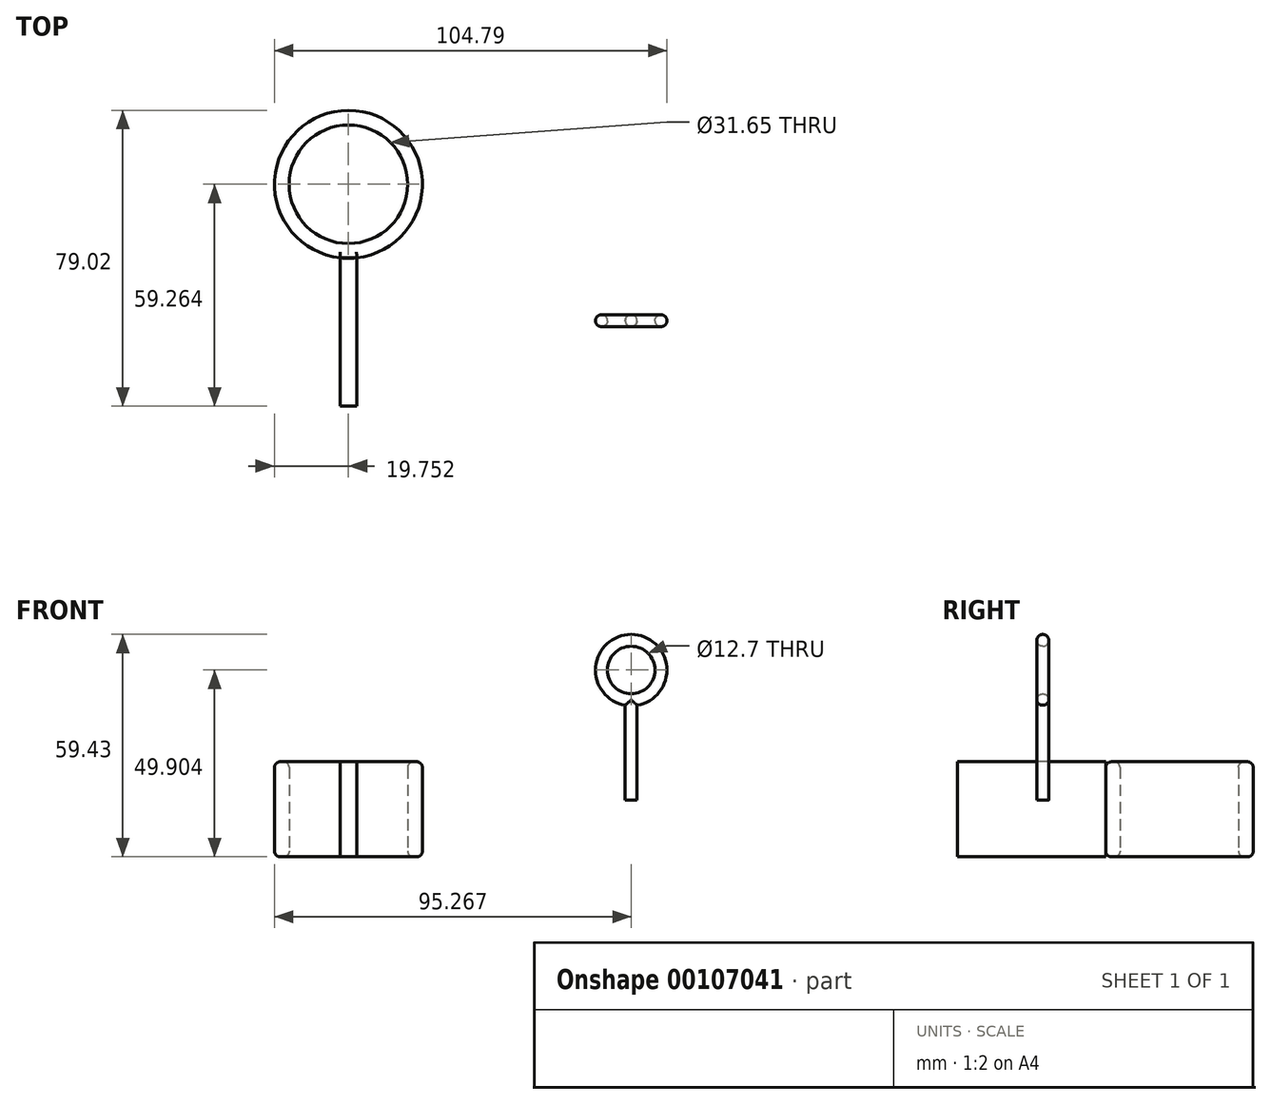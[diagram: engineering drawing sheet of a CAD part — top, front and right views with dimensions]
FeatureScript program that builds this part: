
annotation { "Feature Type Name" : "Feature", "Feature Type Description" : "" }
export const myFeature = defineFeature(function(context is Context, id is Id, definition is map)
    precondition{}
    {
        {
            var Q0;
            Q0=qCreatedBy(makeId("Top.planeOp"),FACE);
            var sketch = newSketch(context, id + "F0", { "sketchPlane" : qUnion([Q0])});
            skCircle(sketch, "E0", {"center": v(-17.5, 34.85) * mm, "radius": 15.83 * mm});
            skCircle(sketch, "E1", {"center": v(-17.5, 34.85) * mm, "radius": 19.76 * mm});
            skLineSegment(sketch, "E2.bottom", {"start": v(-19.74, 15.23) * mm, "end": v(-15.26, 15.23) * mm});
            skLineSegment(sketch, "E2.top", {"start": v(-19.74, -24.41) * mm, "end": v(-15.26, -24.41) * mm});
            skLineSegment(sketch, "E2.left", {"start": v(-19.74, 15.23) * mm, "end": v(-19.74, -24.41) * mm});
            skLineSegment(sketch, "E2.right", {"start": v(-15.26, 15.23) * mm, "end": v(-15.26, -24.41) * mm});
            skSolve(sketch);
        }
        {
            var Q0;
            Q0=makeQuery(id+"F0.imprint","IMPRINT",FACE,{"disambiguationData":[TD([[makeQuery(id+"F0.imprint","IMPRINT",EDGE,{"derivedFrom":sQuery(id+"F0.wireOp",EDGE,"E2.top")}),1.0]])]});
            var Q1;
            Q1=makeQuery(id+"F0.imprint","IMPRINT",FACE,{"disambiguationData":[TD([[makeQuery(id+"F0.imprint","IMPRINT",EDGE,{"derivedFrom":sQuery(id+"F0.wireOp",EDGE,"E0")}),-1.0]])]});
            extrude(context, id + "F1", {"entities" : qUnion([Q0, Q1]), "depth" : 25.4 * mm});
        }
        {
            var Q0;
            Q0=makeQuery(id+"F1.opExtrude","CAP_FACE",FACE,{"disambiguationData":[OSD([sQuery(id+"F0.wireOp",EDGE,"E0"),sQuery(id+"F0.wireOp",EDGE,"E1"),sQuery(id+"F0.wireOp",EDGE,"E2.bottom")])],"isStart":true});
            var Q1;
            Q1=makeQuery(id+"F1.opExtrude","CAP_EDGE",EDGE,{"disambiguationData":[OSD([sQuery(id+"F0.wireOp",EDGE,"E0")])],"isStart":false});
            var Q2;
            Q2=makeQuery(id+"F1.opExtrude","CAP_FACE",FACE,{"disambiguationData":[OSD([sQuery(id+"F0.wireOp",EDGE,"E0"),sQuery(id+"F0.wireOp",EDGE,"E1"),sQuery(id+"F0.wireOp",EDGE,"E2.bottom")])],"isStart":false});
            fillet(context, id + "F2", {"entities" : qUnion([Q0, Q1, Q2]), "radius" : 1.53 * mm, "tangentPropagation" : true, "allowEdgeOverflow" : false});
        }
        {
            var Q0;
            Q0=qCreatedBy(makeId("Front.planeOp"),FACE);
            var sketch = newSketch(context, id + "F3", { "sketchPlane" : qUnion([Q0])});
            skCircle(sketch, "E3", {"center": v(58.02, 49.9) * mm, "radius": 6.35 * mm});
            skCircle(sketch, "E4", {"center": v(58.02, 49.9) * mm, "radius": 9.53 * mm});
            skLineSegment(sketch, "E5", {"start": v(56.43, 40.51) * mm, "end": v(56.43, 15.11) * mm});
            skLineSegment(sketch, "E6", {"start": v(56.43, 15.11) * mm, "end": v(59.6, 15.11) * mm});
            skLineSegment(sketch, "E7", {"start": v(59.6, 15.11) * mm, "end": v(59.6, 40.51) * mm});
            skSolve(sketch);
        }
        {
            var Q0;
            {var subQ0=sQuery(id+"F3.wireOp",EDGE,"E5");Q0=makeQuery(id+"F3.imprint","IMPRINT",FACE,{"disambiguationData":[TD([[makeQuery(id+"F3.imprint","IMPRINT",EDGE,{"derivedFrom":subQ0}),1.0]])]});}
            var Q1;
            Q1=makeQuery(id+"F3.imprint","IMPRINT",FACE,{"disambiguationData":[TD([[makeQuery(id+"F3.imprint","IMPRINT",EDGE,{"derivedFrom":sQuery(id+"F3.wireOp",EDGE,"E3")}),-1.0]])]});
            extrude(context, id + "F4", {"entities" : qUnion([Q0, Q1]), "depth" : 3.17 * mm});
        }
        {
            var Q0;
            Q0=makeQuery(id+"F4.opExtrude","CAP_EDGE",EDGE,{"disambiguationData":[OSD([sQuery(id+"F3.wireOp",EDGE,"E3")])],"isStart":false});
            var Q1;
            Q1=makeQuery(id+"F4.opExtrude","CAP_EDGE",EDGE,{"disambiguationData":[OSD([sQuery(id+"F3.wireOp",EDGE,"E4")])],"isStart":false});
            var Q2;
            Q2=makeQuery(id+"F4.opExtrude","CAP_EDGE",EDGE,{"disambiguationData":[OSD([sQuery(id+"F3.wireOp",EDGE,"E7")])],"isStart":false});
            var Q3;
            Q3=makeQuery(id+"F4.opExtrude","CAP_EDGE",EDGE,{"disambiguationData":[OSD([sQuery(id+"F3.wireOp",EDGE,"E5")])],"isStart":false});
            var Q4;
            Q4=makeQuery(id+"F4.opExtrude","CAP_EDGE",EDGE,{"disambiguationData":[OSD([sQuery(id+"F3.wireOp",EDGE,"E4")])],"isStart":true});
            var Q5;
            Q5=makeQuery(id+"F4.opExtrude","CAP_EDGE",EDGE,{"disambiguationData":[OSD([sQuery(id+"F3.wireOp",EDGE,"E3")])],"isStart":true});
            var Q6;
            Q6=makeQuery(id+"F4.opExtrude","CAP_EDGE",EDGE,{"disambiguationData":[OSD([sQuery(id+"F3.wireOp",EDGE,"E7")])],"isStart":true});
            var Q7;
            Q7=makeQuery(id+"F4.opExtrude","CAP_EDGE",EDGE,{"disambiguationData":[OSD([sQuery(id+"F3.wireOp",EDGE,"E5")])],"isStart":true});
            fillet(context, id + "F5", {"entities" : qUnion([Q0, Q1, Q2, Q3, Q4, Q5, Q6, Q7]), "radius" : 1.57 * mm, "tangentPropagation" : true, "allowEdgeOverflow" : false});
        }
    });
